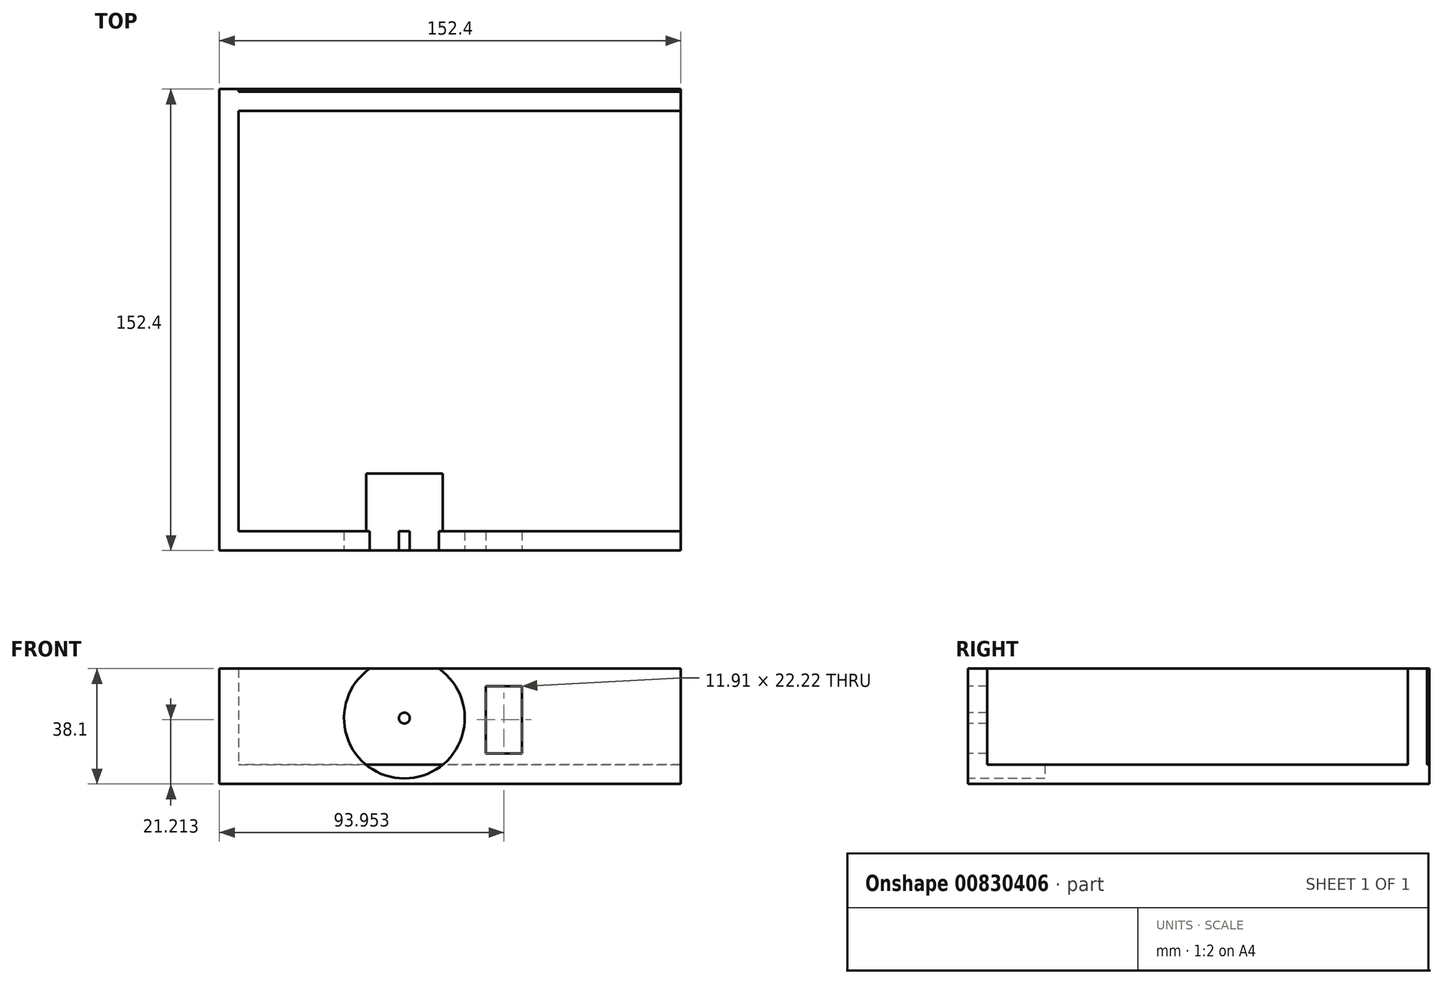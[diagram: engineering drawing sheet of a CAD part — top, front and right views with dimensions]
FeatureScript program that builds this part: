
annotation { "Feature Type Name" : "Feature", "Feature Type Description" : "" }
export const myFeature = defineFeature(function(context is Context, id is Id, definition is map)
    precondition{}
    {
        {
            var Q0;
            Q0=qCreatedBy(makeId("Top.planeOp"),FACE);
            var sketch = newSketch(context, id + "F0", { "sketchPlane" : qUnion([Q0])});
            skLineSegment(sketch, "E0.bottom", {"start": v(0, 0) * mm, "end": v(152.4, 0) * mm});
            skLineSegment(sketch, "E0.top", {"start": v(0, 152.4) * mm, "end": v(152.4, 152.4) * mm});
            skLineSegment(sketch, "E0.left", {"start": v(0, 0) * mm, "end": v(0, 152.4) * mm});
            skLineSegment(sketch, "E0.right", {"start": v(152.4, 0) * mm, "end": v(152.4, 152.4) * mm});
            skSolve(sketch);
        }
        {
            var Q0;
            Q0=makeQuery(id+"F0.imprint","IMPRINT",FACE,{"disambiguationData":[TD([[makeQuery(id+"F0.imprint","IMPRINT",EDGE,{"derivedFrom":sQuery(id+"F0.wireOp",EDGE,"E0.bottom")}),1.0]])]});
            extrude(context, id + "F1", {"entities" : qUnion([Q0]), "depth" : 6.35 * mm, "offsetDistance" : 25.4 * mm});
        }
        {
            var Q0;
            Q0=qCreatedBy(makeId("Top.planeOp"),FACE);
            var sketch = newSketch(context, id + "F2", { "sketchPlane" : qUnion([Q0])});
            skLineSegment(sketch, "E1.bottom", {"start": v(0, 0) * mm, "end": v(152.4, 0) * mm});
            skLineSegment(sketch, "E1.top", {"start": v(0, 6.35) * mm, "end": v(152.4, 6.35) * mm});
            skLineSegment(sketch, "E1.left", {"start": v(0, 0) * mm, "end": v(0, 6.35) * mm});
            skLineSegment(sketch, "E1.right", {"start": v(152.4, 0) * mm, "end": v(152.4, 6.35) * mm});
            skSolve(sketch);
        }
        {
            var Q0;
            Q0 = qSketchRegion(id + "F2", true);
            extrude(context, id + "F3", {"entities" : qUnion([Q0]), "operationType" : NewBodyOperationType.ADD, "depth" : 38.1 * mm, "offsetDistance" : 25.4 * mm});
        }
        {
            var Q0;
            Q0=qCreatedBy(makeId("Top.planeOp"),FACE);
            var sketch = newSketch(context, id + "F4", { "sketchPlane" : qUnion([Q0])});
            skLineSegment(sketch, "E2.bottom", {"start": v(152.4, 151.6) * mm, "end": v(0, 151.6) * mm});
            skLineSegment(sketch, "E2.top", {"start": v(152.4, 145.25) * mm, "end": v(0, 145.25) * mm});
            skLineSegment(sketch, "E2.left", {"start": v(152.4, 151.6) * mm, "end": v(152.4, 145.25) * mm});
            skLineSegment(sketch, "E2.right", {"start": v(0, 151.6) * mm, "end": v(0, 145.25) * mm});
            skSolve(sketch);
        }
        {
            var Q0;
            Q0 = qSketchRegion(id + "F4", true);
            extrude(context, id + "F5", {"entities" : qUnion([Q0]), "operationType" : NewBodyOperationType.ADD, "depth" : 38.1 * mm, "offsetDistance" : 25.4 * mm});
        }
        {
            var Q0;
            Q0=qCreatedBy(makeId("Top.planeOp"),FACE);
            var sketch = newSketch(context, id + "F6", { "sketchPlane" : qUnion([Q0])});
            skLineSegment(sketch, "E3.bottom", {"start": v(0, 152.4) * mm, "end": v(6.35, 152.4) * mm});
            skLineSegment(sketch, "E3.top", {"start": v(0, 0) * mm, "end": v(6.35, 0) * mm});
            skLineSegment(sketch, "E3.left", {"start": v(0, 152.4) * mm, "end": v(0, 0) * mm});
            skLineSegment(sketch, "E3.right", {"start": v(6.35, 152.4) * mm, "end": v(6.35, 0) * mm});
            skSolve(sketch);
        }
        {
            var Q0;
            Q0 = qSketchRegion(id + "F6", true);
            extrude(context, id + "F7", {"entities" : qUnion([Q0]), "operationType" : NewBodyOperationType.ADD, "depth" : 38.1 * mm, "offsetDistance" : 25.4 * mm});
        }
        {
            var Q0;
            Q0=qCreatedBy(makeId("Front.planeOp"),FACE);
            var sketch = newSketch(context, id + "F8", { "sketchPlane" : qUnion([Q0])});
            skLineSegment(sketch, "E4.bottom", {"start": v(88, 32.33) * mm, "end": v(99.9, 32.33) * mm});
            skLineSegment(sketch, "E4.top", {"start": v(88, 10.1) * mm, "end": v(99.9, 10.1) * mm});
            skLineSegment(sketch, "E4.left", {"start": v(88, 32.33) * mm, "end": v(88, 10.1) * mm});
            skLineSegment(sketch, "E4.right", {"start": v(99.9, 32.33) * mm, "end": v(99.9, 10.1) * mm});
            skPoint(sketch, "E5", {"position": v(88, 21.21) * mm});
            skCircle(sketch, "E6", {"center": v(61.06, 21.77) * mm, "radius": 19.94 * mm});
            skCircle(sketch, "E7", {"center": v(61.06, 21.77) * mm, "radius": 1.79 * mm});
            skSolve(sketch);
        }
        {
            var Q0;
            Q0 = qSketchRegion(id + "F8", true);
            extrude(context, id + "F9", {"entities" : qUnion([Q0]), "operationType" : NewBodyOperationType.REMOVE, "oppositeDirection" : true, "depth" : 25.4 * mm, "offsetDistance" : 25.4 * mm});
        }
        {
            var Q0;
            Q0=makeQuery(id+"F8.imprint","IMPRINT",FACE,{"disambiguationData":[TD([[makeQuery(id+"F8.imprint","IMPRINT",EDGE,{"derivedFrom":sQuery(id+"F8.wireOp",EDGE,"E4.bottom")}),-1.0]])]});
            extrude(context, id + "F10", {"entities" : qUnion([Q0]), "operationType" : NewBodyOperationType.REMOVE, "oppositeDirection" : true, "depth" : 25.4 * mm, "offsetDistance" : 25.4 * mm});
        }
    });
